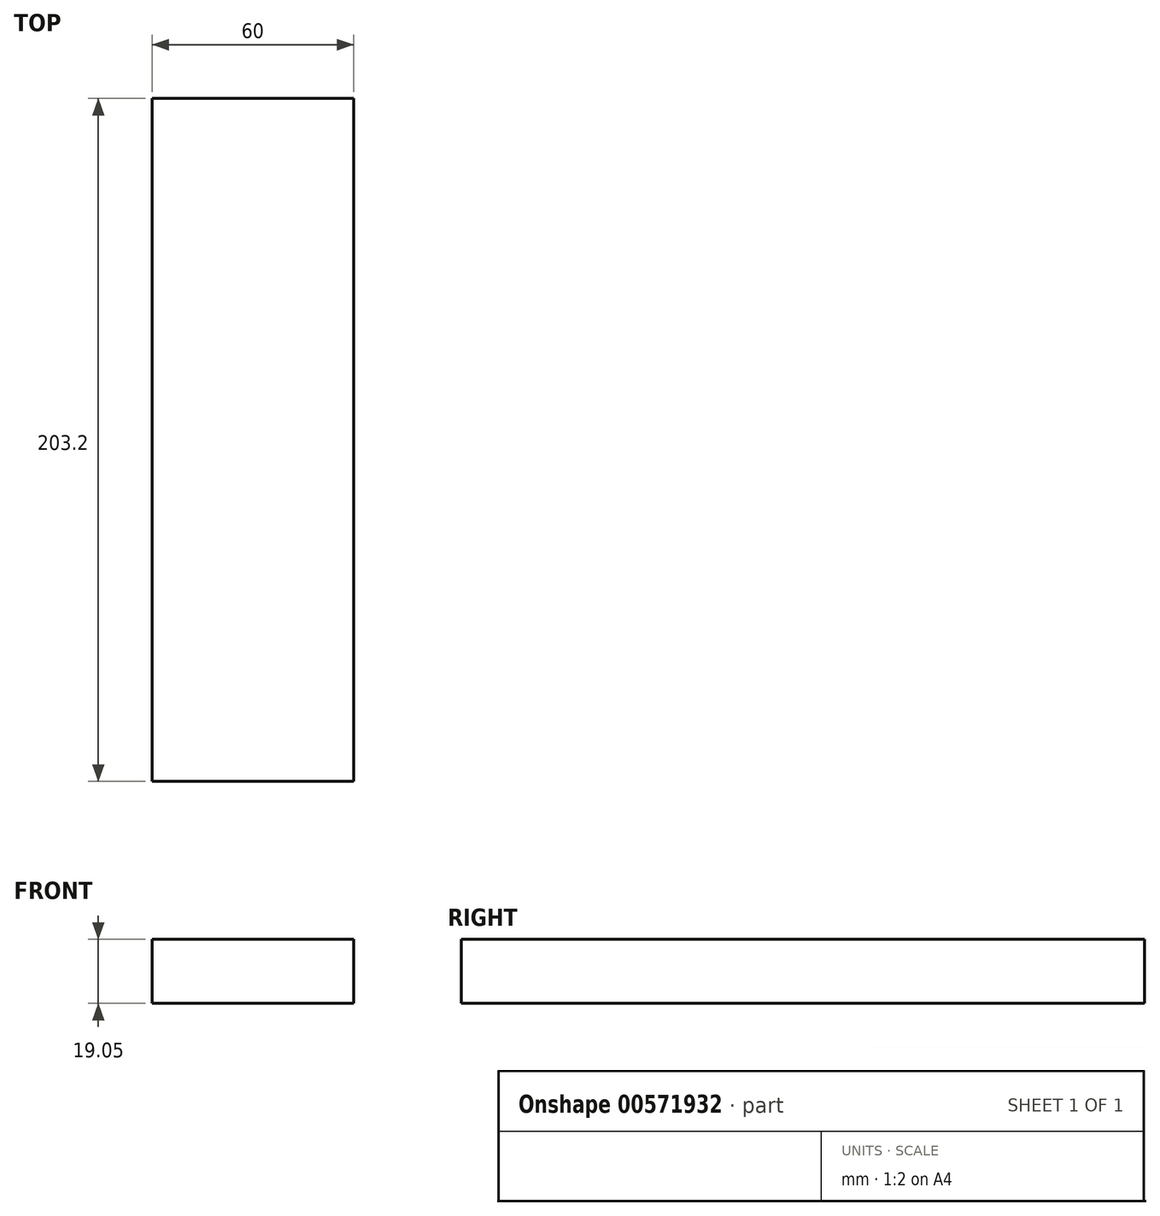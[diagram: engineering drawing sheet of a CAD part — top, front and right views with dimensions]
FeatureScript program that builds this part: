
annotation { "Feature Type Name" : "Feature", "Feature Type Description" : "" }
export const myFeature = defineFeature(function(context is Context, id is Id, definition is map)
    precondition{}
    {
        {
            var Q0;
            Q0=qCreatedBy(makeId("Top.planeOp"),FACE);
            var sketch = newSketch(context, id + "F0", { "sketchPlane" : qUnion([Q0])});
            skLineSegment(sketch, "E0", {"start": v(-87, -113.5) * mm, "end": v(-27, -113.5) * mm});
            skLineSegment(sketch, "E1", {"start": v(-27, -113.5) * mm, "end": v(-27, 89.7) * mm});
            skLineSegment(sketch, "E2", {"start": v(-27, 89.7) * mm, "end": v(-87, 89.7) * mm});
            skLineSegment(sketch, "E3", {"start": v(-87, 89.7) * mm, "end": v(-87, -113.5) * mm});
            skSolve(sketch);
        }
        {
            var Q0;
            Q0=qSketchRegion(id+"F0",true);
            extrude(context, id + "F1", {"entities" : qUnion([Q0]), "depth" : 19.05 * mm, "offsetDistance" : 25.4 * mm});
        }
    });
